# Revit family: CWW
name_source: partatom
category: Lighting Fixtures
units: mm (PartAtom-declared; Revit-internal decimal feet)

## family parameters
Cut with Voids When Loaded = No
Host = Face
Light Source = Yes
OmniClass Number = 23.80.70.11
OmniClass Title = Luminaries for Internal Lighting
Part Type = Normal
Room Calculation Point = No
Round Connector Dimension = Use Diameter
Shared = No

## types (6) — shared parameters
Ceiling Type = Grid
Color Filter = 16777215
Default Elevation = 4' - 0"
Description = Contemporary LED Wall Wash
Dimming Lamp Color Temperature Shift = <None>
Emit Shape Visible in Rendering = No
Emit from Rectangle Width = 0' - 3 1/2"
Lamp = LED Lamp
Load Classification = Lighting
Manufacturer = Columbia Lighting
Material Finish = Paint - White
Model = CWW
Opal lens = Glass
Photometric Web Notes = More IES files Download Photometric Web Link
Power Factor = 1
Tilt Angle = -90.00°
URL = https://www.currentlighting.com
Voltage = 120 V
Warranty = Five year warranty
Wattage Comments = 20W-23.2W

## per-type parameters (varying)
| type | Apparent Load | Distribution | Emit from Rectangle Length | Length | Lumen Output | Photometric Web File | Watts |
| CWW4-40XWG-2WW-EDU | 25 VA | Double Wallwash | 3' - 10" | 4' - 0" | Extra Low Watt | CWW4-40XWG-2WW-EDU.ies | 25 W |
| CWW4-50MLG-1WW-EDU | 50 VA | Asymmetric Wallwash | 3' - 10" | 4' - 0" | Medium Lumen | CWW4-50MLG-1WW-EDU.ies | 50 W |
| CWW4-50XWG-1WR-EDU | 25 VA | Asymmetric Wallwash with Roomside | 3' - 10" | 4' - 0" | Extra Low Watt | CWW4-50XWG-1WR-EDU.ies | 25 W |
| CWW2-30VWG-2WW-EDU | 15 VA | Double Wallwash | 1' - 10" | 2' - 0" | Very Low Watt | CWW2-30VWG-2WW-EDU.ies | 15 W |
| CWW2-30MWG-1WW-EDU | 20 VA | Asymmetric Wallwash | 1' - 10" | 2' - 0" | Medium Low Watt | CWW2-30MWG-1WW-EDU.ies | 20 W |
| CWW2-30LWG-1WR-EDU | 27 VA | Asymmetric Wallwash with Roomside | 1' - 10" | 2' - 0" | Low Watt | 2x4 2Lamp.ies | 27 W |

## geometry (parser evidence)
native form markers: Sweep x4
no freeform markers — native parametric forms only
